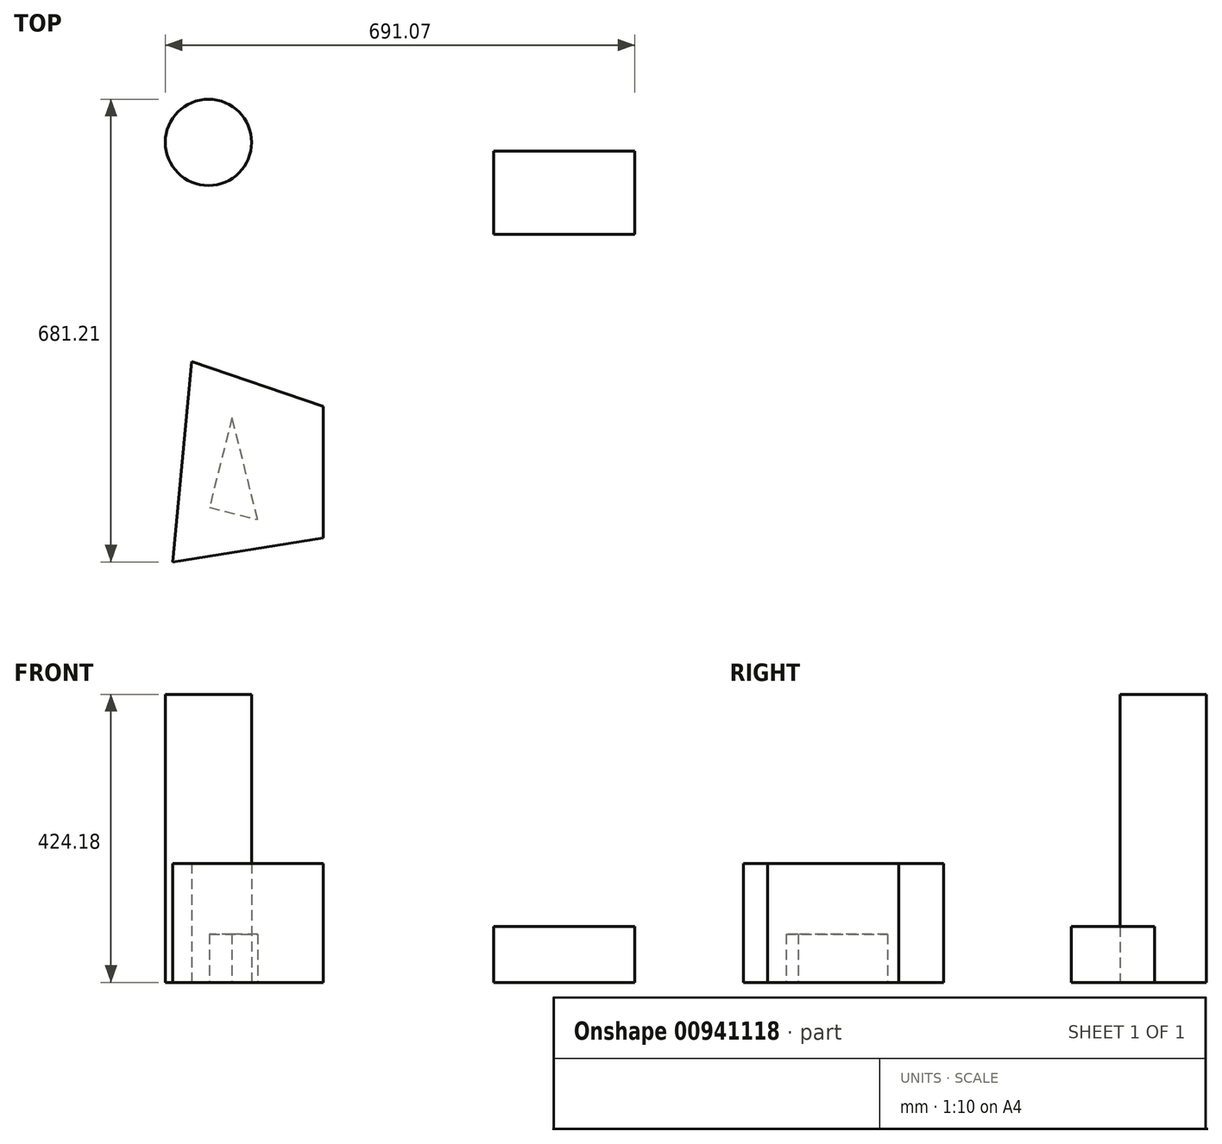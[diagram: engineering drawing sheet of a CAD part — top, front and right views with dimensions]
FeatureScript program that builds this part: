
annotation { "Feature Type Name" : "Feature", "Feature Type Description" : "" }
export const myFeature = defineFeature(function(context is Context, id is Id, definition is map)
    precondition{}
    {
        {
            var Q0;
            Q0=qCreatedBy(makeId("Top.planeOp"),FACE);
            var sketch = newSketch(context, id + "F0", { "sketchPlane" : qUnion([Q0])});
            skCircle(sketch, "E0", {"center": v(-311.54, 245.35) * mm, "radius": 63.5 * mm});
            skLineSegment(sketch, "E1.bottom", {"start": v(108.5, 232.64) * mm, "end": v(316.03, 232.64) * mm});
            skLineSegment(sketch, "E1.top", {"start": v(108.5, 110) * mm, "end": v(316.03, 110) * mm});
            skLineSegment(sketch, "E1.left", {"start": v(108.5, 232.64) * mm, "end": v(108.5, 110) * mm});
            skLineSegment(sketch, "E1.right", {"start": v(316.03, 232.64) * mm, "end": v(316.03, 110) * mm});
            skLineSegment(sketch, "E2", {"start": v(-335.96, -77.57) * mm, "end": v(-142.58, -143.6) * mm});
            skLineSegment(sketch, "E3", {"start": v(-142.58, -143.6) * mm, "end": v(-142.58, -336.98) * mm});
            skLineSegment(sketch, "E4", {"start": v(-142.58, -336.98) * mm, "end": v(-364.26, -372.36) * mm});
            skLineSegment(sketch, "E5", {"start": v(-364.26, -372.36) * mm, "end": v(-335.96, -77.57) * mm});
            skLineSegment(sketch, "E6", {"start": v(-277, -160.1) * mm, "end": v(-310.02, -292.17) * mm});
            skLineSegment(sketch, "E7", {"start": v(-310.02, -292.17) * mm, "end": v(-239, -309.93) * mm});
            skLineSegment(sketch, "E8", {"start": v(-239, -309.93) * mm, "end": v(-277, -160.1) * mm});
            skSolve(sketch);
        }
        {
            var Q0;
            Q0=makeQuery(id+"F0.imprint","IMPRINT",FACE,{"disambiguationData":[TD([[makeQuery(id+"F0.imprint","IMPRINT",EDGE,{"derivedFrom":sQuery(id+"F0.wireOp",EDGE,"E1.bottom")}),-1.0]])]});
            extrude(context, id + "F1", {"entities" : qUnion([Q0]), "depth" : 82.3 * mm, "offsetDistance" : 25.4 * mm});
        }
        {
            var Q0;
            Q0=makeQuery(id+"F0.imprint","IMPRINT",FACE,{"disambiguationData":[TD([[makeQuery(id+"F0.imprint","IMPRINT",EDGE,{"derivedFrom":sQuery(id+"F0.wireOp",EDGE,"E6")}),1.0]])]});
            var Q1;
            Q1=makeQuery(id+"F0.imprint","IMPRINT",FACE,{"disambiguationData":[TD([[makeQuery(id+"F0.imprint","IMPRINT",EDGE,{"derivedFrom":sQuery(id+"F0.wireOp",EDGE,"E2")}),-1.0]])]});
            extrude(context, id + "F2", {"entities" : qUnion([Q0, Q1]), "depth" : 175.26 * mm, "offsetDistance" : 25.4 * mm});
        }
        {
            var Q0;
            Q0=makeQuery(id+"F0.imprint","IMPRINT",FACE,{"disambiguationData":[TD([[makeQuery(id+"F0.imprint","IMPRINT",EDGE,{"derivedFrom":sQuery(id+"F0.wireOp",EDGE,"E0")}),1.0]])]});
            extrude(context, id + "F3", {"entities" : qUnion([Q0]), "depth" : 424.18 * mm, "offsetDistance" : 25.4 * mm});
        }
        {
            var Q0;
            Q0=makeQuery(id+"F0.imprint","IMPRINT",FACE,{"disambiguationData":[TD([[makeQuery(id+"F0.imprint","IMPRINT",EDGE,{"derivedFrom":sQuery(id+"F0.wireOp",EDGE,"E6")}),1.0]])]});
            extrude(context, id + "F4", {"entities" : qUnion([Q0]), "operationType" : NewBodyOperationType.REMOVE, "depth" : 71.12 * mm, "offsetDistance" : 25.4 * mm});
        }
    });
